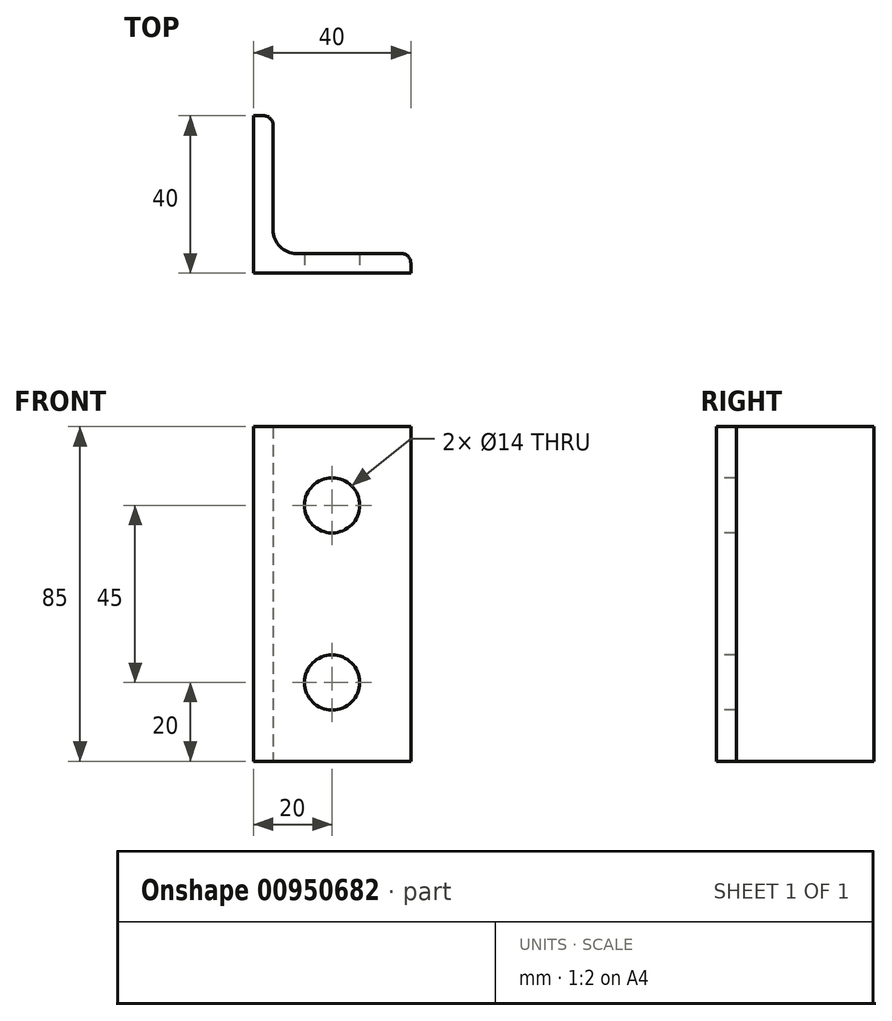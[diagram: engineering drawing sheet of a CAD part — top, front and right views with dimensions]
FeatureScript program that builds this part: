
annotation { "Feature Type Name" : "Feature", "Feature Type Description" : "" }
export const myFeature = defineFeature(function(context is Context, id is Id, definition is map)
    precondition{}
    {
        {
            var Q0;
            Q0=qCreatedBy(makeId("Top.planeOp"),FACE);
            var sketch = newSketch(context, id + "F0", { "sketchPlane" : qUnion([Q0])});
            skLineSegment(sketch, "E0", {"start": v(0, 0) * mm, "end": v(0, 40) * mm});
            skLineSegment(sketch, "E1", {"start": v(0, 40) * mm, "end": v(2.6, 40) * mm});
            skLineSegment(sketch, "E2", {"start": v(5, 37.6) * mm, "end": v(5, 11) * mm});
            skLineSegment(sketch, "E3", {"start": v(11, 5) * mm, "end": v(37.6, 5) * mm});
            skLineSegment(sketch, "E4", {"start": v(40, 2.6) * mm, "end": v(40, 0) * mm});
            skLineSegment(sketch, "E5", {"start": v(40, 0) * mm, "end": v(0, 0) * mm});
            skPoint(sketch, "E6.visualSharp", {"position": v(5, 5) * mm});
            skArc(sketch, "E6.filletArc", {"start": v(5, 11) * mm, "mid": v(6.76, 6.76) * mm, "end": v(11, 5) * mm});
            skPoint(sketch, "E7.visualSharp", {"position": v(5, 40) * mm});
            skArc(sketch, "E7.filletArc", {"start": v(5, 37.6) * mm, "mid": v(4.3, 39.3) * mm, "end": v(2.6, 40) * mm});
            skPoint(sketch, "E8.visualSharp", {"position": v(40, 5) * mm});
            skArc(sketch, "E8.filletArc", {"start": v(40, 2.6) * mm, "mid": v(39.3, 4.3) * mm, "end": v(37.6, 5) * mm});
            skSolve(sketch);
        }
        {
            var Q0;
            Q0=makeQuery(id+"F0.imprint","IMPRINT",FACE,{"disambiguationData":[TD([[makeQuery(id+"F0.imprint","IMPRINT",EDGE,{"derivedFrom":sQuery(id+"F0.wireOp",EDGE,"E0")}),-1.0]])]});
            extrude(context, id + "F1", {"entities" : qUnion([Q0]), "depth" : 85 * mm, "offsetDistance" : 25 * mm});
        }
        {
            var Q0;
            Q0=makeQuery(id+"F1.opExtrude","SWEPT_FACE",FACE,{"disambiguationData":[OSD([sQuery(id+"F0.wireOp",EDGE,"E5")])]});
            var sketch = newSketch(context, id + "F2", { "sketchPlane" : qUnion([Q0])});
            skCircle(sketch, "E9", {"center": v(20, 20) * mm, "radius": 7 * mm});
            skCircle(sketch, "E10", {"center": v(20, 65) * mm, "radius": 7 * mm});
            skSolve(sketch);
        }
        {
            var Q0;
            Q0=makeQuery(id+"F2.imprint","IMPRINT",FACE,{"disambiguationData":[TD([[makeQuery(id+"F2.imprint","IMPRINT",EDGE,{"derivedFrom":sQuery(id+"F2.wireOp",EDGE,"E10")}),1.0]])]});
            var Q1;
            Q1=makeQuery(id+"F2.imprint","IMPRINT",FACE,{"disambiguationData":[TD([[makeQuery(id+"F2.imprint","IMPRINT",EDGE,{"derivedFrom":sQuery(id+"F2.wireOp",EDGE,"E9")}),1.0]])]});
            extrude(context, id + "F3", {"entities" : qUnion([Q0, Q1]), "operationType" : NewBodyOperationType.REMOVE, "endBound" : BoundingType.THROUGH_ALL, "oppositeDirection" : true, "depth" : 25 * mm, "offsetDistance" : 25 * mm});
        }
    });
